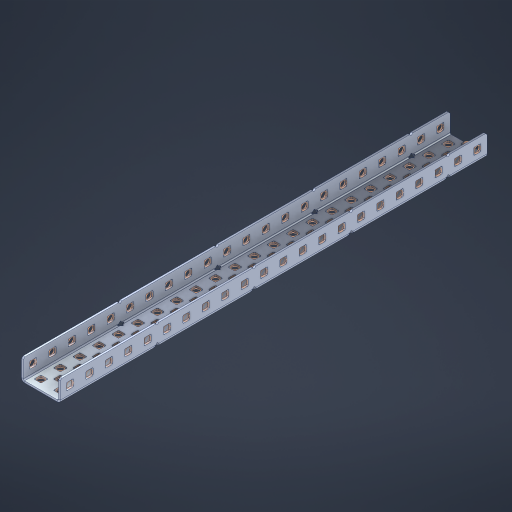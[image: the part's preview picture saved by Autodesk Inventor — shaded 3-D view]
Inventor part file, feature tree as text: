
AUTODESK INVENTOR PART (.ipt)
format: ipt  version: 2023 (Build 270158000, 158)  size: 1,503,744 bytes
history: native  units: in
note: dims shown in document units (in); Inventor stores cm internally (conversion verified against a paired STEP export)
features: other x117, extrude x108, sheet_metal_op x11, sketch x10, pattern_linear x2, mirror x1, chamfer x1
ambient origin geometry x8: Origin, YZ Plane, XZ Plane, XY Plane, X Axis, Y Axis, Z Axis, Center Point
bodies: Solid1 (feature_tree), Body (feature_tree)
feature tree (250):
  sheet_metal_op  "Flanges"
  other  "Flange Pattern Plane"
  other  "Flange Pattern Sketch"
  sheet_metal_op  "Flange Pattern"
  sheet_metal_op  "Body Pattern"
  pattern_linear  "Center Pattern"  Spacing1=0.0469in  [1 undecoded]
  other  "Arc Length"
  mirror  "Notch Mirror"
  pattern_linear  "Notch Pattern"  Spacing1=0.182in  [1 undecoded]
  chamfer  "End Chamfer"
  extrude  "Half Cut"  Depth=0.02in
  sketch  "Sketch1"  dims[d0=1.0in]
  other  "Plate1"
  sketch  "Sketch2"  dims[d1=11.0in]
  other  "Plate2"
  sheet_metal_op  "Bend1"
  sheet_metal_op  "Corner1"
  sketch  "Sketch3"  dims[d2=0.0469in]
  sketch  "Sketch7"  dims[d3=0.0469in]
  other  "Srf1"
  other  "Srf2"
  sketch  "Sketch8"  dims[d4=0.0234in]
  sketch  "Sketch9"  dims[d5=0.0938in]
  other  "Srf91"
  sheet_metal_op  "Body Pattern Sketch"
  other  "Srf92"
  sketch  "Sketch13"  dims[d6=0.0469in]
  sketch  "Sketch14"  dims[d7=0.5in d8=90.0deg d9=0.0312in]
  sketch  "Sketch15"  dims[d10=0.1875in]
  sketch  "Sketch16"  dims[d11=0.0469in d12=0.0469in d16=0.182in d17=0.02in d18=0.0469in d19=0.0in d20=0.25in d21=0.25in d38=8.6614in d40=0.5in d41=0.7874in d43=1.0in d46=0.172in d47=1.0in d48=0.0in d49=0.182in d50=0.02in d51=0.25in d52=0.25in d53=0.0469in d54=0.0in d55=0.172in d56=1.0in d57=0.0in d58=0.25in d60=8.6614in d62=0.5in d63=0.7874in d65=0.5in d85=0.1227in d86=0.1659in d88=0.04in d89=0.0469in d90=0.0in d91=0.04in d92=0.0491in d95=2.5in d96=0.04in d97=0.25in d98=45.0deg d99=0.25in d100=0.5in d101=0.0in d102=2.497in d106=0.182in d107=0.02in d108=0.5in d109=0.5in d110=0.0469in d111=0.0in d112=0.172in d113=0.5in d114=0.0in d117=0.5in d118=0.5in d119=0.5in]
  other  "Srf786"
  other  "Srf823"
  other  "Srf824"
  other  "Srf825"
  other  "Srf826"
  other  "Srf827"
  other  "Srf828"
  other  "Srf829"
  other  "Srf856"
  other  "Srf857"
  other  "Srf858"
  other  "Srf859"
  other  "Srf860"
  other  "Srf861"
  other  "Srf862"
  other  "Srf889"
  other  "Srf890"
  other  "Srf891"
  other  "Srf892"
  other  "Srf893"
  other  "Srf894"
  other  "Srf895"
  other  "Srf896"
  other  "Srf922"
  other  "Srf923"
  other  "Srf924"
  other  "Srf925"
  other  "Srf926"
  other  "Srf959"
  other  "Srf960"
  other  "Srf961"
  other  "Srf962"
  other  "Srf963"
  other  "Srf996"
  other  "Srf997"
  other  "Srf998"
  other  "Srf999"
  other  "Srf1000"
  other  "Srf1143"
  other  "Srf1144"
  other  "Srf1145"
  other  "Srf1146"
  other  "Srf1147"
  other  "Srf1148"
  other  "Srf1149"
  other  "Srf1150"
  other  "Srf1151"
  other  "Srf1152"
  other  "Srf1153"
  other  "Srf1154"
  other  "Srf1155"
  other  "Srf1156"
  other  "Srf1157"
  other  "Srf1158"
  other  "Srf1159"
  other  "Srf1160"
  other  "Srf1161"
  other  "Srf1162"
  other  "Srf1163"
  other  "Srf1164"
  other  "Srf1165"
  other  "Srf1166"
  other  "Srf1167"
  other  "Srf1168"
  other  "Srf1169"
  other  "Srf1170"
  other  "Srf1171"
  other  "Srf1172"
  other  "Srf1199"
  other  "Srf1200"
  other  "Srf1201"
  other  "Srf1202"
  other  "Srf1203"
  other  "Srf1204"
  other  "Srf1205"
  other  "Srf1206"
  other  "Srf1207"
  other  "Srf1208"
  other  "Srf1209"
  other  "Srf1210"
  other  "Srf1211"
  other  "Srf1212"
  other  "Srf1213"
  other  "Srf1214"
  other  "Srf1215"
  other  "Srf1216"
  other  "Srf1217"
  other  "Srf1218"
  other  "Srf1219"
  other  "Srf1220"
  other  "Srf1221"
  other  "Srf1222"
  other  "Srf1223"
  other  "Srf1224"
  other  "Srf1225"
  other  "Srf1226"
  other  "Srf1227"
  other  "Srf1228"
  other  "Srf1255"
  other  "Srf1256"
  other  "Srf1257"
  other  "Srf1258"
  other  "Srf1259"
  other  "Srf1260"
  other  "Srf1261"
  other  "Srf1262"
  sheet_metal_op  "Flange Stamp"
  sheet_metal_op  "Flange Circle"
  sheet_metal_op  "Body Stamp"
  sheet_metal_op  "Body Circle"
  other  "Center Stamp"
  other  "Center Circle"
  sheet_metal_op  "Notch"
  extrude  "ExtrusionSrf2"  Depth=0.0469in
  extrude  "ExtrusionSrf92"  TaperAngle=0.0deg  [1 undecoded]
  extrude  "ExtrusionSrf823"  Depth=0.5in
  extrude  "ExtrusionSrf824"  Depth=0.5in
  extrude  "ExtrusionSrf825"  Depth=0.5in
  extrude  "ExtrusionSrf826"  Depth=0.5in
  extrude  "ExtrusionSrf827"  Depth=1.0in TaperAngle=0.0deg
  extrude  "ExtrusionSrf828"  Depth=0.5in
  extrude  "ExtrusionSrf829"  Depth=0.02in
  extrude  "ExtrusionSrf856"  Depth=0.5in
  extrude  "ExtrusionSrf857"  Depth=0.5in
  extrude  "ExtrusionSrf858"  Depth=0.0469in
  extrude  "ExtrusionSrf859"  TaperAngle=0.0deg  [1 undecoded]
  extrude  "ExtrusionSrf860"  Depth=0.5in
  extrude  "ExtrusionSrf861"  Depth=1.0in TaperAngle=0.0deg
  extrude  "ExtrusionSrf862"  Depth=0.5in
  extrude  "ExtrusionSrf889"  Depth=0.5in
  extrude  "ExtrusionSrf890"  Depth=0.5in
  extrude  "ExtrusionSrf891"  Depth=0.5in
  extrude  "ExtrusionSrf892"  Depth=0.5in
  extrude  "ExtrusionSrf893"  Depth=0.5in
  extrude  "ExtrusionSrf894"  Depth=0.0469in
  extrude  "ExtrusionSrf895"  TaperAngle=0.0deg  [1 undecoded]
  extrude  "ExtrusionSrf896"  Depth=0.5in
  extrude  "ExtrusionSrf922"  Depth=0.5in
  extrude  "ExtrusionSrf923"  Depth=2.5in
  extrude  "ExtrusionSrf924"  Depth=0.5in TaperAngle=45.0deg
  extrude  "ExtrusionSrf925"  Depth=0.5in
  extrude  "ExtrusionSrf926"  Depth=0.5in TaperAngle=0.0deg
  extrude  "ExtrusionSrf959"  Depth=0.5in
  extrude  "ExtrusionSrf960"  Depth=0.5in
  extrude  "ExtrusionSrf961"  Depth=0.02in
  extrude  "ExtrusionSrf962"  Depth=0.5in
  extrude  "ExtrusionSrf963"  Depth=0.5in
  extrude  "ExtrusionSrf996"  Depth=0.0469in
  extrude  "ExtrusionSrf997"  TaperAngle=0.0deg  [1 undecoded]
  extrude  "ExtrusionSrf998"  Depth=0.5in
  extrude  "ExtrusionSrf999"  Depth=0.5in TaperAngle=0.0deg
  extrude  "ExtrusionSrf1000"  Depth=0.5in
  extrude  "ExtrusionSrf1143"  Depth=0.5in
  extrude  "ExtrusionSrf1144"  Depth=0.5in
  extrude  "ExtrusionSrf1145"  [1 undecoded]
  extrude  "ExtrusionSrf1146"  [1 undecoded]
  extrude  "ExtrusionSrf1147"  [1 undecoded]
  extrude  "ExtrusionSrf1148"  [1 undecoded]
  extrude  "ExtrusionSrf1149"  [1 undecoded]
  extrude  "ExtrusionSrf1150"  [1 undecoded]
  extrude  "ExtrusionSrf1151"  [1 undecoded]
  extrude  "ExtrusionSrf1152"  [1 undecoded]
  extrude  "ExtrusionSrf1153"  [1 undecoded]
  extrude  "ExtrusionSrf1154"  [1 undecoded]
  extrude  "ExtrusionSrf1155"  [1 undecoded]
  extrude  "ExtrusionSrf1156"  [1 undecoded]
  extrude  "ExtrusionSrf1157"  [1 undecoded]
  extrude  "ExtrusionSrf1158"  [1 undecoded]
  extrude  "ExtrusionSrf1159"  [1 undecoded]
  extrude  "ExtrusionSrf1160"  [1 undecoded]
  extrude  "ExtrusionSrf1161"  [1 undecoded]
  extrude  "ExtrusionSrf1162"  [1 undecoded]
  extrude  "ExtrusionSrf1163"  [1 undecoded]
  extrude  "ExtrusionSrf1164"  [1 undecoded]
  extrude  "ExtrusionSrf1165"  [1 undecoded]
  extrude  "ExtrusionSrf1166"  [1 undecoded]
  extrude  "ExtrusionSrf1167"  [1 undecoded]
  extrude  "ExtrusionSrf1168"  [1 undecoded]
  extrude  "ExtrusionSrf1169"  [1 undecoded]
  extrude  "ExtrusionSrf1170"  [1 undecoded]
  extrude  "ExtrusionSrf1171"  [1 undecoded]
  extrude  "ExtrusionSrf1172"  [1 undecoded]
  extrude  "ExtrusionSrf1199"  [1 undecoded]
  extrude  "ExtrusionSrf1200"  [1 undecoded]
  extrude  "ExtrusionSrf1201"  [1 undecoded]
  extrude  "ExtrusionSrf1202"  [1 undecoded]
  extrude  "ExtrusionSrf1203"  [1 undecoded]
  extrude  "ExtrusionSrf1204"  [1 undecoded]
  extrude  "ExtrusionSrf1205"  [1 undecoded]
  extrude  "ExtrusionSrf1206"  [1 undecoded]
  extrude  "ExtrusionSrf1207"  [1 undecoded]
  extrude  "ExtrusionSrf1208"  [1 undecoded]
  extrude  "ExtrusionSrf1209"  [1 undecoded]
  extrude  "ExtrusionSrf1210"  [1 undecoded]
  extrude  "ExtrusionSrf1211"  [1 undecoded]
  extrude  "ExtrusionSrf1212"  [1 undecoded]
  extrude  "ExtrusionSrf1213"  [1 undecoded]
  extrude  "ExtrusionSrf1214"  [1 undecoded]
  extrude  "ExtrusionSrf1215"  [1 undecoded]
  extrude  "ExtrusionSrf1216"  [1 undecoded]
  extrude  "ExtrusionSrf1217"  [1 undecoded]
  extrude  "ExtrusionSrf1218"  [1 undecoded]
  extrude  "ExtrusionSrf1219"  [1 undecoded]
  extrude  "ExtrusionSrf1220"  [1 undecoded]
  extrude  "ExtrusionSrf1221"  [1 undecoded]
  extrude  "ExtrusionSrf1222"  [1 undecoded]
  extrude  "ExtrusionSrf1223"  [1 undecoded]
  extrude  "ExtrusionSrf1224"  [1 undecoded]
  extrude  "ExtrusionSrf1225"  [1 undecoded]
  extrude  "ExtrusionSrf1226"  [1 undecoded]
  extrude  "ExtrusionSrf1227"  [1 undecoded]
  extrude  "ExtrusionSrf1228"  [1 undecoded]
  extrude  "ExtrusionSrf1255"  [1 undecoded]
  extrude  "ExtrusionSrf1256"  [1 undecoded]
  extrude  "ExtrusionSrf1257"  [1 undecoded]
  extrude  "ExtrusionSrf1258"  [1 undecoded]
  extrude  "ExtrusionSrf1259"  [1 undecoded]
  extrude  "ExtrusionSrf1260"  [1 undecoded]
  extrude  "ExtrusionSrf1261"  [1 undecoded]
  extrude  "ExtrusionSrf1262"  [1 undecoded]
note: 72 required parameter values undecoded (feature->parameter linkage not recoverable at this tier; creation-order binding heuristic only, values carry confidence <= 0.55)
